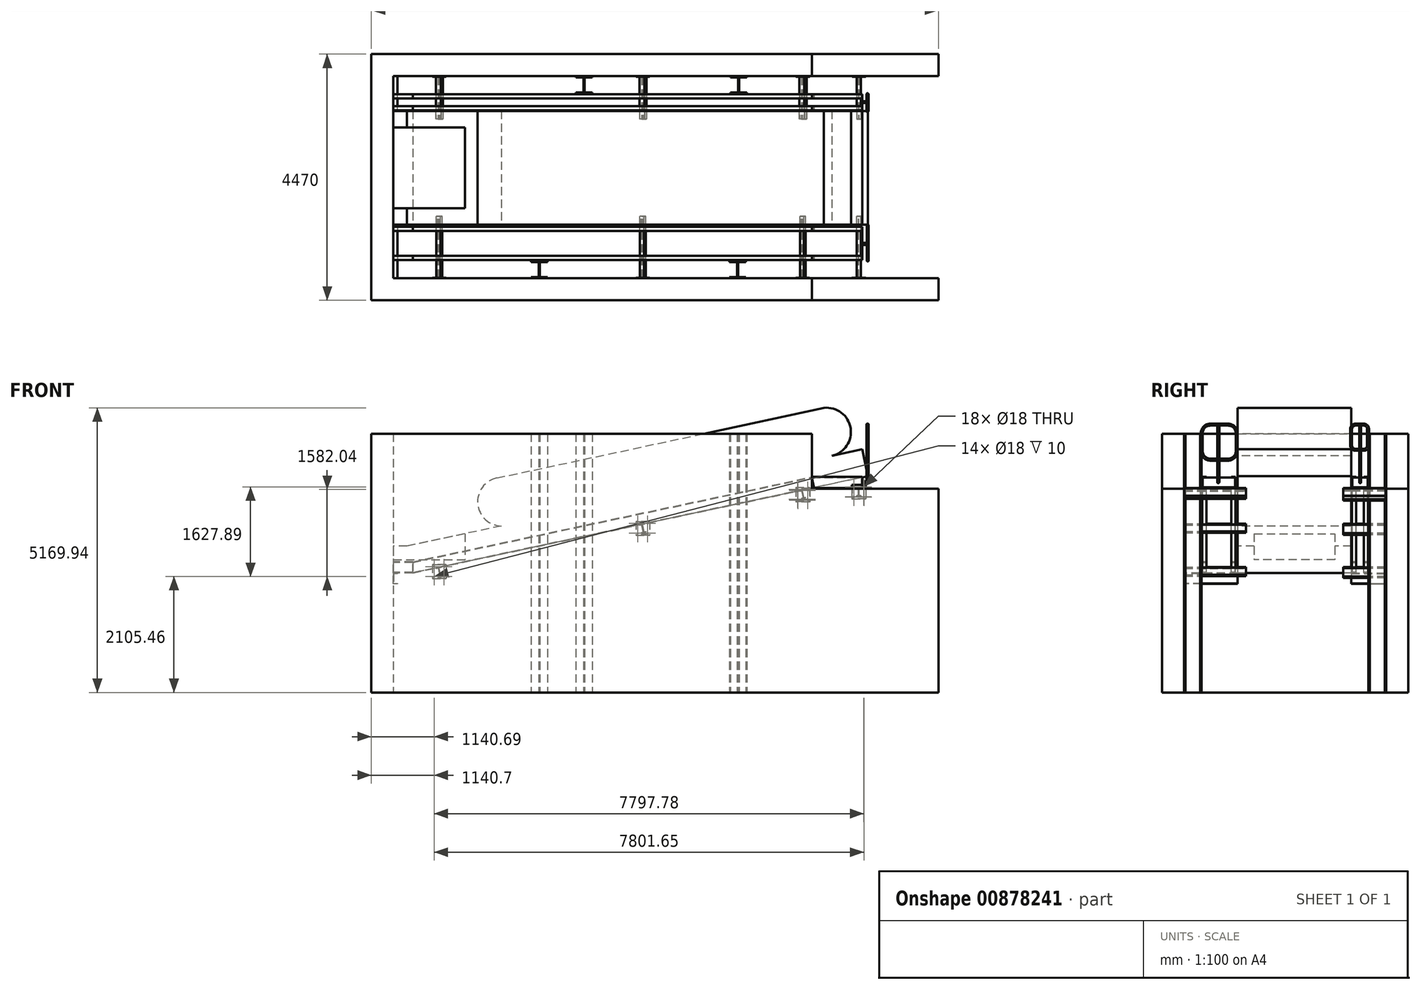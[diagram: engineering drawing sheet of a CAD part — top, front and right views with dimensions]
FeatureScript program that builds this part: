
annotation { "Feature Type Name" : "Feature", "Feature Type Description" : "" }
export const myFeature = defineFeature(function(context is Context, id is Id, definition is map)
    precondition{}
    {
        {
            var Q0;
            Q0=qCreatedBy(makeId("Top.planeOp"),FACE);
            var sketch = newSketch(context, id + "F0", { "sketchPlane" : qUnion([Q0])});
            skLineSegment(sketch, "E0", {"start": v(4950, 1835) * mm, "end": v(-4950, 1835) * mm});
            skLineSegment(sketch, "E1", {"start": v(-4950, 1835) * mm, "end": v(-4950, -1835) * mm});
            skLineSegment(sketch, "E2", {"start": v(-4950, -1835) * mm, "end": v(4950, -1835) * mm});
            skLineSegment(sketch, "E3", {"start": v(4950, -1835) * mm, "end": v(4950, -2235) * mm});
            skLineSegment(sketch, "E4", {"start": v(4950, -2235) * mm, "end": v(-5350, -2235) * mm});
            skLineSegment(sketch, "E5", {"start": v(-5350, -2235) * mm, "end": v(-5350, 2235) * mm});
            skLineSegment(sketch, "E6", {"start": v(-5350, 2235) * mm, "end": v(4950, 2235) * mm});
            skLineSegment(sketch, "E7", {"start": v(4950, 2235) * mm, "end": v(4950, 1835) * mm});
            skSolve(sketch);
        }
        {
            var Q0;
            Q0=qSketchRegion(id+"F0",true);
            extrude(context, id + "F1", {"entities" : qUnion([Q0]), "depth" : 4700 * mm, "offsetDistance" : 25 * mm});
        }
        {
            var Q0;
            Q0=makeQuery(id+"F1.opExtrude","SWEPT_FACE",FACE,{"disambiguationData":[OSD([sQuery(id+"F0.wireOp",EDGE,"E4")])]});
            var sketch = newSketch(context, id + "F2", { "sketchPlane" : qUnion([Q0])});
            skLineSegment(sketch, "E8", {"start": v(2650, 4700) * mm, "end": v(2650, 3700) * mm});
            skLineSegment(sketch, "E9", {"start": v(2650, 3700) * mm, "end": v(4950, 3700) * mm});
            skLineSegment(sketch, "E10", {"start": v(4950, 3700) * mm, "end": v(4950, 4700) * mm});
            skLineSegment(sketch, "E11", {"start": v(4950, 4700) * mm, "end": v(2650, 4700) * mm});
            skSolve(sketch);
        }
        {
            var Q0;
            Q0=qSketchRegion(id+"F2",true);
            extrude(context, id + "F3", {"entities" : qUnion([Q0]), "operationType" : NewBodyOperationType.REMOVE, "endBound" : BoundingType.THROUGH_ALL, "oppositeDirection" : true, "depth" : 25 * mm, "offsetDistance" : 25 * mm});
        }
        {
            var Q0;
            Q0=makeQuery(id+"F1.opExtrude","SWEPT_FACE",FACE,{"disambiguationData":[OSD([sQuery(id+"F0.wireOp",EDGE,"E2")])]});
            cPlane(context, id + "F4", {"entities" : qUnion([Q0]), "cplaneType" : CPlaneType.OFFSET, "offset" : 975 * mm, "width" : 150 * mm, "height" : 150 * mm});
        }
        {
            var Q0;
            Q0=qCreatedBy(id+"F4.planeOp",FACE);
            var sketch = newSketch(context, id + "F5", { "sketchPlane" : qUnion([Q0])});
            skLineSegment(sketch, "E12", {"start": v(0, 0) * mm, "end": v(4950, 0) * mm, "construction": true});
            skLineSegment(sketch, "E13", {"start": v(4950, 0) * mm, "end": v(4950, 2170) * mm, "construction": true});
            skLineSegment(sketch, "E14", {"start": v(3073.33, 3893.76) * mm, "end": v(-2866.18, 5167.23) * mm});
            skArc(sketch, "E15", {"start": v(2794.82, 3064.72) * mm, "mid": v(3398.25, 3323.3) * mm, "end": v(3073.33, 3893.76) * mm});
            skArc(sketch, "E16", {"start": v(-2866.18, 5167.23) * mm, "mid": v(-3350.27, 4800.3) * mm, "end": v(-3008.93, 4297.83) * mm});
            skLineSegment(sketch, "E17", {"start": v(-3008.93, 4297.83) * mm, "end": v(-3560.65, 4415.1) * mm});
            skLineSegment(sketch, "E18", {"start": v(-3560.65, 4415.1) * mm, "end": v(-3664.6, 3926.03) * mm});
            skLineSegment(sketch, "E19", {"start": v(-3664.6, 3926.03) * mm, "end": v(4600, 2170) * mm});
            skLineSegment(sketch, "E20", {"start": v(2794.82, 3064.72) * mm, "end": v(4703.92, 2658.93) * mm});
            skLineSegment(sketch, "E21", {"start": v(4950, 2658.93) * mm, "end": v(4950, 2170) * mm});
            skLineSegment(sketch, "E22", {"start": v(4703.92, 2658.93) * mm, "end": v(4950, 2658.93) * mm});
            skLineSegment(sketch, "E23", {"start": v(4600, 2170) * mm, "end": v(4950, 2170) * mm});
            skSolve(sketch);
        }
        {
            var Q0;
            Q0=qSketchRegion(id+"F5",true);
            extrude(context, id + "F6", {"entities" : qUnion([Q0]), "depth" : 2065 * mm, "offsetDistance" : 25 * mm});
        }
        {
            var Q0;
            Q0=qCreatedBy(makeId("Top.planeOp"),FACE);
            var sketch = newSketch(context, id + "F7", { "sketchPlane" : qUnion([Q0])});
            skLineSegment(sketch, "E24", {"start": v(-2450, -1835) * mm, "end": v(-2450, -1810) * mm});
            skLineSegment(sketch, "E25", {"start": v(-2450, -1810) * mm, "end": v(-2310, -1810) * mm});
            skLineSegment(sketch, "E26", {"start": v(-2290, -1540) * mm, "end": v(-2290, -1810) * mm});
            skLineSegment(sketch, "E27", {"start": v(-2290, -1810) * mm, "end": v(-2150, -1810) * mm});
            skLineSegment(sketch, "E28", {"start": v(-2150, -1810) * mm, "end": v(-2150, -1835) * mm});
            skLineSegment(sketch, "E29", {"start": v(-2150, -1835) * mm, "end": v(-2450, -1835) * mm});
            skLineSegment(sketch, "E30", {"start": v(-2310, -1810) * mm, "end": v(-2310, -1540) * mm});
            skLineSegment(sketch, "E31", {"start": v(-2310, -1540) * mm, "end": v(-2450, -1540) * mm});
            skLineSegment(sketch, "E32", {"start": v(-2450, -1540) * mm, "end": v(-2450, -1515) * mm});
            skLineSegment(sketch, "E33", {"start": v(-2150, -1515) * mm, "end": v(-2450, -1515) * mm});
            skLineSegment(sketch, "E34", {"start": v(-2290, -1540) * mm, "end": v(-2150, -1540) * mm});
            skLineSegment(sketch, "E35", {"start": v(-2150, -1540) * mm, "end": v(-2150, -1515) * mm});
            skLineSegment(sketch, "E36.MirrorCS", {"start": v(1150, -1540) * mm, "end": v(1150, -1515) * mm});
            skLineSegment(sketch, "E37.MirrorCS", {"start": v(1450, -1540) * mm, "end": v(1450, -1515) * mm});
            skLineSegment(sketch, "E38.MirrorCS", {"start": v(1150, -1810) * mm, "end": v(1150, -1835) * mm});
            skLineSegment(sketch, "E39.MirrorCS", {"start": v(1450, -1835) * mm, "end": v(1450, -1810) * mm});
            skLineSegment(sketch, "E40.MirrorCS", {"start": v(1290, -1540) * mm, "end": v(1150, -1540) * mm});
            skLineSegment(sketch, "E41.MirrorCS", {"start": v(1290, -1540) * mm, "end": v(1290, -1810) * mm});
            skLineSegment(sketch, "E42.MirrorCS", {"start": v(1310, -1540) * mm, "end": v(1450, -1540) * mm});
            skLineSegment(sketch, "E43.MirrorCS", {"start": v(1290, -1810) * mm, "end": v(1150, -1810) * mm});
            skLineSegment(sketch, "E44.MirrorCS", {"start": v(1450, -1810) * mm, "end": v(1310, -1810) * mm});
            skLineSegment(sketch, "E45.MirrorCS", {"start": v(1150, -1835) * mm, "end": v(1450, -1835) * mm});
            skLineSegment(sketch, "E46.MirrorCS", {"start": v(1150, -1515) * mm, "end": v(1450, -1515) * mm});
            skLineSegment(sketch, "E47.MirrorCS", {"start": v(1310, -1810) * mm, "end": v(1310, -1540) * mm});
            skLineSegment(sketch, "E48", {"start": v(0, 0) * mm, "end": v(-354.85, 0) * mm, "construction": true});
            skLineSegment(sketch, "E49", {"start": v(-1640, 1515) * mm, "end": v(-1640, 1540) * mm});
            skLineSegment(sketch, "E50", {"start": v(-1640, 1540) * mm, "end": v(-1500, 1540) * mm});
            skLineSegment(sketch, "E51", {"start": v(-1480, 1810) * mm, "end": v(-1480, 1540) * mm});
            skLineSegment(sketch, "E52", {"start": v(-1480, 1540) * mm, "end": v(-1340, 1540) * mm});
            skLineSegment(sketch, "E53", {"start": v(-1340, 1540) * mm, "end": v(-1340, 1515) * mm});
            skLineSegment(sketch, "E54", {"start": v(-1340, 1515) * mm, "end": v(-1640, 1515) * mm});
            skLineSegment(sketch, "E55", {"start": v(-1500, 1540) * mm, "end": v(-1500, 1810) * mm});
            skLineSegment(sketch, "E56", {"start": v(-1500, 1810) * mm, "end": v(-1640, 1810) * mm});
            skLineSegment(sketch, "E57", {"start": v(-1640, 1810) * mm, "end": v(-1640, 1835) * mm});
            skLineSegment(sketch, "E58", {"start": v(-1340, 1835) * mm, "end": v(-1640, 1835) * mm});
            skLineSegment(sketch, "E59", {"start": v(-1480, 1810) * mm, "end": v(-1340, 1810) * mm});
            skLineSegment(sketch, "E60", {"start": v(-1340, 1810) * mm, "end": v(-1340, 1835) * mm});
            skLineSegment(sketch, "E61", {"start": v(1170, 1515) * mm, "end": v(1170, 1540) * mm});
            skLineSegment(sketch, "E62", {"start": v(1170, 1540) * mm, "end": v(1310, 1540) * mm});
            skLineSegment(sketch, "E63", {"start": v(1330, 1810) * mm, "end": v(1330, 1540) * mm});
            skLineSegment(sketch, "E64", {"start": v(1330, 1540) * mm, "end": v(1470, 1540) * mm});
            skLineSegment(sketch, "E65", {"start": v(1470, 1540) * mm, "end": v(1470, 1515) * mm});
            skLineSegment(sketch, "E66", {"start": v(1470, 1515) * mm, "end": v(1170, 1515) * mm});
            skLineSegment(sketch, "E67", {"start": v(1310, 1540) * mm, "end": v(1310, 1810) * mm});
            skLineSegment(sketch, "E68", {"start": v(1310, 1810) * mm, "end": v(1170, 1810) * mm});
            skLineSegment(sketch, "E69", {"start": v(1170, 1810) * mm, "end": v(1170, 1835) * mm});
            skLineSegment(sketch, "E70", {"start": v(1470, 1835) * mm, "end": v(1170, 1835) * mm});
            skLineSegment(sketch, "E71", {"start": v(1330, 1810) * mm, "end": v(1470, 1810) * mm});
            skLineSegment(sketch, "E72", {"start": v(1470, 1810) * mm, "end": v(1470, 1835) * mm});
            skSolve(sketch);
        }
        {
            var Q0;
            Q0=qSketchRegion(id+"F7",true);
            extrude(context, id + "F8", {"entities" : qUnion([Q0]), "depth" : 4700 * mm, "offsetDistance" : 25 * mm});
        }
        {
            var Q0;
            Q0=makeQuery(id+"F6.opExtrude","CAP_FACE",FACE,{"disambiguationData":[OSD([sQuery(id+"F5.wireOp",EDGE,"E14"),sQuery(id+"F5.wireOp",EDGE,"E15"),sQuery(id+"F5.wireOp",EDGE,"E16"),sQuery(id+"F5.wireOp",EDGE,"oLefBTFz-qkPp-oevc-OMQC-yi734GtDL7CI"),sQuery(id+"F5.wireOp",EDGE,"Q5l5viEM-SpAK-wrV8-5FxA-7hyHcSo3zPGG"),sQuery(id+"F5.wireOp",EDGE,"E17"),sQuery(id+"F5.wireOp",EDGE,"Mw7AiCCQ-qxsM-Rx6K-VWYf-NFiuKVvHO99K"),sQuery(id+"F5.wireOp",EDGE,"wAlzpoZe-HTRn-fX5u-Gcly-RZiGOCXCuHdc")])],"isStart":true});
            var sketch = newSketch(context, id + "F9", { "sketchPlane" : qUnion([Q0])});
            skLineSegment(sketch, "E73", {"start": v(-434.88, 3054.99) * mm, "end": v(-400.65, 3062.26) * mm});
            skLineSegment(sketch, "E74", {"start": v(-400.65, 3062.26) * mm, "end": v(-399.2, 3055.41) * mm});
            skLineSegment(sketch, "E75", {"start": v(-399.2, 3055.41) * mm, "end": v(-433.43, 3048.14) * mm});
            skLineSegment(sketch, "E76", {"start": v(-433.43, 3048.14) * mm, "end": v(-405.16, 2915.11) * mm});
            skLineSegment(sketch, "E77", {"start": v(-405.16, 2915.11) * mm, "end": v(-370.93, 2922.38) * mm});
            skLineSegment(sketch, "E78", {"start": v(-370.93, 2922.38) * mm, "end": v(-369.47, 2915.54) * mm});
            skLineSegment(sketch, "E79", {"start": v(-369.47, 2915.54) * mm, "end": v(-442.83, 2899.95) * mm});
            skLineSegment(sketch, "E80", {"start": v(-442.83, 2899.95) * mm, "end": v(-444.29, 2906.8) * mm});
            skLineSegment(sketch, "E81", {"start": v(-444.29, 2906.8) * mm, "end": v(-410.05, 2914.07) * mm});
            skLineSegment(sketch, "E82", {"start": v(-410.05, 2914.07) * mm, "end": v(-438.32, 3047.1) * mm});
            skLineSegment(sketch, "E83", {"start": v(-438.32, 3047.1) * mm, "end": v(-472.55, 3039.83) * mm});
            skLineSegment(sketch, "E84", {"start": v(-472.55, 3039.83) * mm, "end": v(-474, 3046.67) * mm});
            skLineSegment(sketch, "E85", {"start": v(-474, 3046.67) * mm, "end": v(-400.65, 3062.26) * mm});
            skLineSegment(sketch, "E86.MirrorCS", {"start": v(-4128.54, 2263.02) * mm, "end": v(-4094.3, 2270.3) * mm});
            skLineSegment(sketch, "E87.MirrorCS", {"start": v(-4167.66, 2254.7) * mm, "end": v(-4133.43, 2261.98) * mm});
            skLineSegment(sketch, "E88.MirrorCS", {"start": v(-4169.12, 2261.55) * mm, "end": v(-4167.66, 2254.7) * mm});
            skLineSegment(sketch, "E89.MirrorCS", {"start": v(-4105.16, 2128.95) * mm, "end": v(-4139.4, 2121.67) * mm});
            skLineSegment(sketch, "E90.MirrorCS", {"start": v(-4134.88, 2268.83) * mm, "end": v(-4169.12, 2261.55) * mm});
            skLineSegment(sketch, "E91.MirrorCS", {"start": v(-4139.4, 2121.67) * mm, "end": v(-4137.94, 2114.83) * mm});
            skLineSegment(sketch, "E92.MirrorCS", {"start": v(-4066.04, 2137.26) * mm, "end": v(-4100.27, 2129.99) * mm});
            skLineSegment(sketch, "E93.MirrorCS", {"start": v(-4095.76, 2277.14) * mm, "end": v(-4169.12, 2261.55) * mm});
            skLineSegment(sketch, "E94.MirrorCS", {"start": v(-4137.94, 2114.83) * mm, "end": v(-4064.58, 2130.42) * mm});
            skLineSegment(sketch, "E95.MirrorCS", {"start": v(-4064.58, 2130.42) * mm, "end": v(-4066.04, 2137.26) * mm});
            skLineSegment(sketch, "E96.MirrorCS", {"start": v(-4094.3, 2270.3) * mm, "end": v(-4095.76, 2277.14) * mm});
            skLineSegment(sketch, "E97.MirrorCS", {"start": v(-4133.43, 2261.98) * mm, "end": v(-4105.16, 2128.95) * mm});
            skLineSegment(sketch, "E98.MirrorCS", {"start": v(-4100.27, 2129.99) * mm, "end": v(-4128.54, 2263.02) * mm});
            skLineSegment(sketch, "E99.MirrorCS", {"start": v(2429.47, 3663.6) * mm, "end": v(2430.93, 3656.75) * mm});
            skLineSegment(sketch, "E100.MirrorCS", {"start": v(2504.3, 3672.34) * mm, "end": v(2502.84, 3679.18) * mm});
            skLineSegment(sketch, "E101.MirrorCS", {"start": v(2430.93, 3656.75) * mm, "end": v(2465.16, 3664.02) * mm});
            skLineSegment(sketch, "E102.MirrorCS", {"start": v(2463.7, 3670.87) * mm, "end": v(2429.47, 3663.6) * mm});
            skLineSegment(sketch, "E103.MirrorCS", {"start": v(2502.84, 3679.18) * mm, "end": v(2429.47, 3663.6) * mm});
            skLineSegment(sketch, "E104.MirrorCS", {"start": v(2459.2, 3523.72) * mm, "end": v(2460.65, 3516.87) * mm});
            skLineSegment(sketch, "E105.MirrorCS", {"start": v(2534.01, 3532.46) * mm, "end": v(2532.56, 3539.3) * mm});
            skLineSegment(sketch, "E106.MirrorCS", {"start": v(2470.05, 3665.06) * mm, "end": v(2504.3, 3672.34) * mm});
            skLineSegment(sketch, "E107.MirrorCS", {"start": v(2460.65, 3516.87) * mm, "end": v(2534.01, 3532.46) * mm});
            skLineSegment(sketch, "E108.MirrorCS", {"start": v(2493.43, 3531) * mm, "end": v(2459.2, 3523.72) * mm});
            skLineSegment(sketch, "E109.MirrorCS", {"start": v(2532.56, 3539.3) * mm, "end": v(2498.32, 3532.03) * mm});
            skLineSegment(sketch, "E110.MirrorCS", {"start": v(2465.16, 3664.02) * mm, "end": v(2493.43, 3531) * mm});
            skLineSegment(sketch, "E111.MirrorCS", {"start": v(2498.32, 3532.03) * mm, "end": v(2470.05, 3665.06) * mm});
            skLineSegment(sketch, "E112", {"start": v(-4134.88, 2268.83) * mm, "end": v(-4134.88, 2268.83) * mm});
            skLineSegment(sketch, "E113", {"start": v(-434.88, 3054.99) * mm, "end": v(-434.88, 3054.99) * mm});
            skLineSegment(sketch, "E114", {"start": v(2463.7, 3670.87) * mm, "end": v(2463.7, 3670.87) * mm});
            skLineSegment(sketch, "E115", {"start": v(3664.6, 3926.03) * mm, "end": v(2664.6, 3926.03) * mm, "construction": true});
            skLineSegment(sketch, "E116", {"start": v(2664.6, 3926.03) * mm, "end": v(2420.07, 3874.07) * mm, "construction": true});
            skLineSegment(sketch, "E117", {"start": v(2420.07, 3874.07) * mm, "end": v(2463.26, 3670.77) * mm, "construction": true});
            skLineSegment(sketch, "E118.MirrorCS", {"start": v(3459.6, 3713.73) * mm, "end": v(3459.6, 3706.73) * mm});
            skLineSegment(sketch, "E119.MirrorCS", {"start": v(3534.6, 3706.73) * mm, "end": v(3534.6, 3713.73) * mm});
            skLineSegment(sketch, "E120.MirrorCS", {"start": v(3459.6, 3706.73) * mm, "end": v(3494.6, 3706.73) * mm});
            skLineSegment(sketch, "E121.MirrorCS", {"start": v(3496.14, 3713.73) * mm, "end": v(3459.6, 3713.73) * mm});
            skLineSegment(sketch, "E122.MirrorCS", {"start": v(3534.6, 3713.73) * mm, "end": v(3459.6, 3713.73) * mm});
            skLineSegment(sketch, "E123.MirrorCS", {"start": v(3459.6, 3570.73) * mm, "end": v(3459.6, 3563.73) * mm});
            skLineSegment(sketch, "E124.MirrorCS", {"start": v(3534.6, 3563.73) * mm, "end": v(3534.6, 3570.73) * mm});
            skLineSegment(sketch, "E125.MirrorCS", {"start": v(3499.6, 3706.73) * mm, "end": v(3534.6, 3706.73) * mm});
            skLineSegment(sketch, "E126.MirrorCS", {"start": v(3459.6, 3563.73) * mm, "end": v(3534.6, 3563.73) * mm});
            skLineSegment(sketch, "E127.MirrorCS", {"start": v(3494.6, 3570.73) * mm, "end": v(3459.6, 3570.73) * mm});
            skLineSegment(sketch, "E128.MirrorCS", {"start": v(3534.6, 3570.73) * mm, "end": v(3499.6, 3570.73) * mm});
            skLineSegment(sketch, "E129.MirrorCS", {"start": v(3499.6, 3570.73) * mm, "end": v(3499.6, 3706.73) * mm});
            skLineSegment(sketch, "E130", {"start": v(3494.6, 3706.73) * mm, "end": v(3494.6, 3570.73) * mm});
            skSolve(sketch);
        }
        {
            var Q0;
            Q0 = qSketchRegion(id + "F9", true);
            extrude(context, id + "F10", {"entities" : qUnion([Q0]), "operationType" : NewBodyOperationType.ADD, "depth" : 965 * mm, "offsetDistance" : 25 * mm, "hasSecondDirection" : true, "secondDirectionOppositeDirection" : true, "secondDirectionDepth" : 150 * mm});
        }
        {
            var Q0;
            Q0=makeQuery(id+"F10.opExtrude","CAP_FACE",FACE,{"disambiguationData":[OSD([sQuery(id+"F9.wireOp",EDGE,"E99.MirrorCS"),sQuery(id+"F9.wireOp",EDGE,"E100.MirrorCS"),sQuery(id+"F9.wireOp",EDGE,"E101.MirrorCS"),sQuery(id+"F9.wireOp",EDGE,"E103.MirrorCS"),sQuery(id+"F9.wireOp",EDGE,"E104.MirrorCS"),sQuery(id+"F9.wireOp",EDGE,"E105.MirrorCS"),sQuery(id+"F9.wireOp",EDGE,"E106.MirrorCS"),sQuery(id+"F9.wireOp",EDGE,"E107.MirrorCS"),sQuery(id+"F9.wireOp",EDGE,"E108.MirrorCS"),sQuery(id+"F9.wireOp",EDGE,"E109.MirrorCS"),sQuery(id+"F9.wireOp",EDGE,"E110.MirrorCS"),sQuery(id+"F9.wireOp",EDGE,"E111.MirrorCS")])],"isStart":false});
            var sketch = newSketch(context, id + "F11", { "sketchPlane" : qUnion([Q0])});
            skLineSegment(sketch, "E131.bottom", {"start": v(2354.3, 3722.5) * mm, "end": v(2604.3, 3722.5) * mm});
            skLineSegment(sketch, "E131.top", {"start": v(2354.3, 3472.5) * mm, "end": v(2604.3, 3472.5) * mm});
            skLineSegment(sketch, "E131.left", {"start": v(2354.3, 3722.5) * mm, "end": v(2354.3, 3472.5) * mm});
            skLineSegment(sketch, "E131.right", {"start": v(2604.3, 3722.5) * mm, "end": v(2604.3, 3472.5) * mm});
            skLineSegment(sketch, "E132", {"start": v(2479.3, 3597.5) * mm, "end": v(2479.3, 3576.9) * mm, "construction": true});
            skLineSegment(sketch, "E133", {"start": v(2479.3, 3597.5) * mm, "end": v(2510.05, 3597.5) * mm, "construction": true});
            skCircle(sketch, "E134", {"center": v(2389.3, 3687.5) * mm, "radius": 9 * mm});
            skCircle(sketch, "E135", {"center": v(2389.3, 3507.5) * mm, "radius": 9 * mm});
            skCircle(sketch, "E136", {"center": v(2569.3, 3687.5) * mm, "radius": 9 * mm});
            skCircle(sketch, "E137", {"center": v(2569.3, 3507.5) * mm, "radius": 9 * mm});
            skLineSegment(sketch, "E138.bottom", {"start": v(-549.18, 3105.59) * mm, "end": v(-299.18, 3105.59) * mm});
            skLineSegment(sketch, "E138.top", {"start": v(-549.18, 2855.59) * mm, "end": v(-299.18, 2855.59) * mm});
            skLineSegment(sketch, "E138.left", {"start": v(-549.18, 3105.59) * mm, "end": v(-549.18, 2855.59) * mm});
            skLineSegment(sketch, "E138.right", {"start": v(-299.18, 3105.59) * mm, "end": v(-299.18, 2855.59) * mm});
            skLineSegment(sketch, "E139", {"start": v(-424.18, 2980.59) * mm, "end": v(-424.18, 2959.98) * mm, "construction": true});
            skLineSegment(sketch, "E140", {"start": v(-424.18, 2980.59) * mm, "end": v(-393.43, 2980.59) * mm, "construction": true});
            skCircle(sketch, "E141", {"center": v(-514.18, 3070.59) * mm, "radius": 9 * mm});
            skCircle(sketch, "E142", {"center": v(-514.18, 2890.59) * mm, "radius": 9 * mm});
            skCircle(sketch, "E143", {"center": v(-334.18, 3070.59) * mm, "radius": 9 * mm});
            skCircle(sketch, "E144", {"center": v(-334.18, 2890.59) * mm, "radius": 9 * mm});
            skLineSegment(sketch, "E145.bottom", {"start": v(-4244.3, 2320.46) * mm, "end": v(-3994.3, 2320.46) * mm});
            skLineSegment(sketch, "E145.top", {"start": v(-4244.3, 2070.46) * mm, "end": v(-3994.3, 2070.46) * mm});
            skLineSegment(sketch, "E145.left", {"start": v(-4244.3, 2320.46) * mm, "end": v(-4244.3, 2070.46) * mm});
            skLineSegment(sketch, "E145.right", {"start": v(-3994.3, 2320.46) * mm, "end": v(-3994.3, 2070.46) * mm});
            skLineSegment(sketch, "E146", {"start": v(-4119.3, 2195.46) * mm, "end": v(-4119.3, 2174.86) * mm, "construction": true});
            skLineSegment(sketch, "E147", {"start": v(-4119.3, 2195.46) * mm, "end": v(-4088.55, 2195.46) * mm, "construction": true});
            skCircle(sketch, "E148", {"center": v(-4209.3, 2285.46) * mm, "radius": 9 * mm});
            skCircle(sketch, "E149", {"center": v(-4209.3, 2105.46) * mm, "radius": 9 * mm});
            skCircle(sketch, "E150", {"center": v(-4029.3, 2285.46) * mm, "radius": 9 * mm});
            skCircle(sketch, "E151", {"center": v(-4029.3, 2105.46) * mm, "radius": 9 * mm});
            skLineSegment(sketch, "E152.bottom", {"start": v(3373.49, 3768.35) * mm, "end": v(3623.49, 3768.35) * mm});
            skLineSegment(sketch, "E152.top", {"start": v(3373.49, 3518.35) * mm, "end": v(3623.49, 3518.35) * mm});
            skLineSegment(sketch, "E152.left", {"start": v(3373.49, 3768.35) * mm, "end": v(3373.49, 3518.35) * mm});
            skLineSegment(sketch, "E152.right", {"start": v(3623.49, 3768.35) * mm, "end": v(3623.49, 3518.35) * mm});
            skLineSegment(sketch, "E153", {"start": v(3498.49, 3643.35) * mm, "end": v(3498.49, 3622.74) * mm, "construction": true});
            skLineSegment(sketch, "E154", {"start": v(3498.49, 3643.35) * mm, "end": v(3529.24, 3643.35) * mm, "construction": true});
            skCircle(sketch, "E155", {"center": v(3408.49, 3733.35) * mm, "radius": 9 * mm});
            skCircle(sketch, "E156", {"center": v(3408.49, 3553.35) * mm, "radius": 9 * mm});
            skCircle(sketch, "E157", {"center": v(3588.49, 3733.35) * mm, "radius": 9 * mm});
            skCircle(sketch, "E158", {"center": v(3588.49, 3553.35) * mm, "radius": 9 * mm});
            skSolve(sketch);
        }
        {
            var Q0;
            Q0 = qSketchRegion(id + "F11", true);
            extrude(context, id + "F12", {"entities" : qUnion([Q0]), "operationType" : NewBodyOperationType.ADD, "depth" : 10 * mm, "offsetDistance" : 25 * mm});
        }
        {
            var Q0;
            Q0=makeQuery(id+"F6.opExtrude","CAP_FACE",FACE,{"disambiguationData":[OSD([sQuery(id+"F5.wireOp",EDGE,"E14"),sQuery(id+"F5.wireOp",EDGE,"E15"),sQuery(id+"F5.wireOp",EDGE,"E16"),sQuery(id+"F5.wireOp",EDGE,"oLefBTFz-qkPp-oevc-OMQC-yi734GtDL7CI"),sQuery(id+"F5.wireOp",EDGE,"Q5l5viEM-SpAK-wrV8-5FxA-7hyHcSo3zPGG"),sQuery(id+"F5.wireOp",EDGE,"E17"),sQuery(id+"F5.wireOp",EDGE,"Mw7AiCCQ-qxsM-Rx6K-VWYf-NFiuKVvHO99K"),sQuery(id+"F5.wireOp",EDGE,"wAlzpoZe-HTRn-fX5u-Gcly-RZiGOCXCuHdc")])],"isStart":false});
            var sketch = newSketch(context, id + "F13", { "sketchPlane" : qUnion([Q0])});
            skLineSegment(sketch, "E159.MirrorCS", {"start": v(-2511.47, 3682.12) * mm, "end": v(-2513.27, 3673.67) * mm});
            skLineSegment(sketch, "E160.MirrorCS", {"start": v(-2422.67, 3654.4) * mm, "end": v(-2420.87, 3662.86) * mm});
            skLineSegment(sketch, "E161.MirrorCS", {"start": v(-2513.27, 3673.67) * mm, "end": v(-2470.99, 3664.68) * mm});
            skLineSegment(sketch, "E162.MirrorCS", {"start": v(-2548.2, 3509.38) * mm, "end": v(-2550, 3500.92) * mm});
            skLineSegment(sketch, "E163.MirrorCS", {"start": v(-2459.4, 3481.66) * mm, "end": v(-2457.6, 3490.11) * mm});
            skLineSegment(sketch, "E164.MirrorCS", {"start": v(-2464.95, 3663.4) * mm, "end": v(-2422.67, 3654.4) * mm});
            skLineSegment(sketch, "E165.MirrorCS", {"start": v(-2550, 3500.92) * mm, "end": v(-2459.4, 3481.66) * mm});
            skLineSegment(sketch, "E166.MirrorCS", {"start": v(-2505.92, 3500.39) * mm, "end": v(-2548.2, 3509.38) * mm});
            skLineSegment(sketch, "E167.MirrorCS", {"start": v(-2457.6, 3490.11) * mm, "end": v(-2499.88, 3499.1) * mm});
            skLineSegment(sketch, "E168.MirrorCS", {"start": v(-2470.99, 3664.68) * mm, "end": v(-2505.92, 3500.39) * mm});
            skLineSegment(sketch, "E169.MirrorCS", {"start": v(-2499.88, 3499.1) * mm, "end": v(-2464.95, 3663.4) * mm});
            skLineSegment(sketch, "E170", {"start": v(-2511.47, 3682.12) * mm, "end": v(-2420.87, 3662.86) * mm});
            skLineSegment(sketch, "E171.MirrorCS", {"start": v(392.09, 3064.09) * mm, "end": v(390.29, 3055.63) * mm});
            skLineSegment(sketch, "E172.MirrorCS", {"start": v(480.89, 3036.37) * mm, "end": v(482.69, 3044.82) * mm});
            skLineSegment(sketch, "E173.MirrorCS", {"start": v(390.29, 3055.63) * mm, "end": v(432.57, 3046.64) * mm});
            skLineSegment(sketch, "E174.MirrorCS", {"start": v(355.35, 2891.34) * mm, "end": v(353.56, 2882.89) * mm});
            skLineSegment(sketch, "E175.MirrorCS", {"start": v(444.16, 2863.62) * mm, "end": v(445.95, 2872.08) * mm});
            skLineSegment(sketch, "E176.MirrorCS", {"start": v(438.6, 3045.36) * mm, "end": v(480.89, 3036.37) * mm});
            skLineSegment(sketch, "E177.MirrorCS", {"start": v(353.56, 2882.89) * mm, "end": v(444.16, 2863.62) * mm});
            skLineSegment(sketch, "E178.MirrorCS", {"start": v(397.63, 2882.35) * mm, "end": v(355.35, 2891.34) * mm});
            skLineSegment(sketch, "E179.MirrorCS", {"start": v(445.95, 2872.08) * mm, "end": v(403.67, 2881.07) * mm});
            skLineSegment(sketch, "E180.MirrorCS", {"start": v(432.57, 3046.64) * mm, "end": v(397.63, 2882.35) * mm});
            skLineSegment(sketch, "E181.MirrorCS", {"start": v(403.67, 2881.07) * mm, "end": v(438.6, 3045.36) * mm});
            skLineSegment(sketch, "E182", {"start": v(392.09, 3064.09) * mm, "end": v(482.69, 3044.82) * mm});
            skLineSegment(sketch, "E183.MirrorCS", {"start": v(4087.2, 2279.02) * mm, "end": v(4085.4, 2270.57) * mm});
            skLineSegment(sketch, "E184.MirrorCS", {"start": v(4176, 2251.3) * mm, "end": v(4177.8, 2259.76) * mm});
            skLineSegment(sketch, "E185.MirrorCS", {"start": v(4085.4, 2270.57) * mm, "end": v(4127.69, 2261.58) * mm});
            skLineSegment(sketch, "E186.MirrorCS", {"start": v(4050.47, 2106.28) * mm, "end": v(4048.67, 2097.82) * mm});
            skLineSegment(sketch, "E187.MirrorCS", {"start": v(4139.28, 2078.55) * mm, "end": v(4141.07, 2087.01) * mm});
            skLineSegment(sketch, "E188.MirrorCS", {"start": v(4133.73, 2260.3) * mm, "end": v(4176, 2251.3) * mm});
            skLineSegment(sketch, "E189.MirrorCS", {"start": v(4048.67, 2097.82) * mm, "end": v(4139.28, 2078.55) * mm});
            skLineSegment(sketch, "E190.MirrorCS", {"start": v(4092.75, 2097.29) * mm, "end": v(4050.47, 2106.28) * mm});
            skLineSegment(sketch, "E191.MirrorCS", {"start": v(4141.07, 2087.01) * mm, "end": v(4098.82, 2096) * mm});
            skLineSegment(sketch, "E192.MirrorCS", {"start": v(4127.69, 2261.58) * mm, "end": v(4092.75, 2097.29) * mm});
            skLineSegment(sketch, "E193.MirrorCS", {"start": v(4098.82, 2096) * mm, "end": v(4133.73, 2260.3) * mm});
            skLineSegment(sketch, "E194", {"start": v(4087.2, 2279.02) * mm, "end": v(4177.8, 2259.76) * mm});
            skLineSegment(sketch, "E195", {"start": v(-3664.6, 3926.03) * mm, "end": v(-3664.6, 3714) * mm, "construction": true});
            skLineSegment(sketch, "E196", {"start": v(-3664.6, 3714) * mm, "end": v(-3534.6, 3714) * mm, "construction": true});
            skLineSegment(sketch, "E197", {"start": v(-3664.6, 3926.03) * mm, "end": v(-2664.6, 3926.03) * mm, "construction": true});
            skLineSegment(sketch, "E198", {"start": v(-2664.6, 3926.03) * mm, "end": v(-2420.07, 3874.07) * mm, "construction": true});
            skLineSegment(sketch, "E199", {"start": v(-2420.07, 3874.07) * mm, "end": v(-2420.07, 3661.6) * mm, "construction": true});
            skLineSegment(sketch, "E200.MirrorCS", {"start": v(-3534.58, 3713.73) * mm, "end": v(-3534.58, 3706.73) * mm});
            skLineSegment(sketch, "E201.MirrorCS", {"start": v(-3459.58, 3706.72) * mm, "end": v(-3459.58, 3713.72) * mm});
            skLineSegment(sketch, "E202.MirrorCS", {"start": v(-3534.58, 3706.73) * mm, "end": v(-3499.58, 3706.72) * mm});
            skLineSegment(sketch, "E203.MirrorCS", {"start": v(-3498.05, 3713.72) * mm, "end": v(-3534.58, 3713.73) * mm});
            skLineSegment(sketch, "E204.MirrorCS", {"start": v(-3459.58, 3713.72) * mm, "end": v(-3534.58, 3713.73) * mm});
            skLineSegment(sketch, "E205.MirrorCS", {"start": v(-3534.6, 3570.73) * mm, "end": v(-3534.6, 3563.73) * mm});
            skLineSegment(sketch, "E206.MirrorCS", {"start": v(-3459.6, 3563.72) * mm, "end": v(-3459.6, 3570.72) * mm});
            skLineSegment(sketch, "E207.MirrorCS", {"start": v(-3494.58, 3706.72) * mm, "end": v(-3459.58, 3706.72) * mm});
            skLineSegment(sketch, "E208.MirrorCS", {"start": v(-3534.6, 3563.73) * mm, "end": v(-3459.6, 3563.72) * mm});
            skLineSegment(sketch, "E209.MirrorCS", {"start": v(-3499.6, 3570.72) * mm, "end": v(-3534.6, 3570.73) * mm});
            skLineSegment(sketch, "E210.MirrorCS", {"start": v(-3459.6, 3570.72) * mm, "end": v(-3494.6, 3570.72) * mm});
            skLineSegment(sketch, "E211.MirrorCS", {"start": v(-3494.6, 3570.72) * mm, "end": v(-3494.58, 3706.72) * mm});
            skLineSegment(sketch, "E212", {"start": v(-3499.58, 3706.72) * mm, "end": v(-3499.6, 3570.72) * mm});
            skSolve(sketch);
        }
        {
            var Q0;
            Q0 = qSketchRegion(id + "F13", true);
            extrude(context, id + "F14", {"entities" : qUnion([Q0]), "operationType" : NewBodyOperationType.ADD, "depth" : 620 * mm, "offsetDistance" : 25 * mm, "hasSecondDirection" : true, "secondDirectionOppositeDirection" : true, "secondDirectionDepth" : 150 * mm});
        }
        {
            var Q0;
            Q0=makeQuery(id+"F14.opExtrude","CAP_FACE",FACE,{"disambiguationData":[OSD([sQuery(id+"F13.wireOp",EDGE,"E159.MirrorCS"),sQuery(id+"F13.wireOp",EDGE,"E160.MirrorCS"),sQuery(id+"F13.wireOp",EDGE,"E161.MirrorCS"),sQuery(id+"F13.wireOp",EDGE,"E162.MirrorCS"),sQuery(id+"F13.wireOp",EDGE,"E163.MirrorCS"),sQuery(id+"F13.wireOp",EDGE,"E164.MirrorCS"),sQuery(id+"F13.wireOp",EDGE,"E165.MirrorCS"),sQuery(id+"F13.wireOp",EDGE,"E166.MirrorCS"),sQuery(id+"F13.wireOp",EDGE,"E167.MirrorCS"),sQuery(id+"F13.wireOp",EDGE,"E168.MirrorCS"),sQuery(id+"F13.wireOp",EDGE,"E169.MirrorCS"),sQuery(id+"F13.wireOp",EDGE,"E170")])],"isStart":false});
            var sketch = newSketch(context, id + "F15", { "sketchPlane" : qUnion([Q0])});
            skLineSegment(sketch, "E213.bottom", {"start": v(299.18, 3105.59) * mm, "end": v(549.18, 3105.59) * mm});
            skLineSegment(sketch, "E213.top", {"start": v(299.18, 2855.59) * mm, "end": v(549.18, 2855.59) * mm});
            skLineSegment(sketch, "E213.left", {"start": v(299.18, 3105.59) * mm, "end": v(299.18, 2855.59) * mm});
            skLineSegment(sketch, "E213.right", {"start": v(549.18, 3105.59) * mm, "end": v(549.18, 2855.59) * mm});
            skLineSegment(sketch, "E214", {"start": v(424.18, 3031.13) * mm, "end": v(424.18, 2980.59) * mm, "construction": true});
            skLineSegment(sketch, "E215", {"start": v(424.18, 2980.59) * mm, "end": v(470.05, 2980.59) * mm, "construction": true});
            skCircle(sketch, "E216", {"center": v(334.18, 3070.59) * mm, "radius": 9 * mm});
            skCircle(sketch, "E217", {"center": v(334.18, 2890.59) * mm, "radius": 9 * mm});
            skCircle(sketch, "E218", {"center": v(514.18, 3070.59) * mm, "radius": 9 * mm});
            skCircle(sketch, "E219", {"center": v(514.18, 2890.59) * mm, "radius": 9 * mm});
            skLineSegment(sketch, "E220.bottom", {"start": v(3994.3, 2320.46) * mm, "end": v(4244.3, 2320.46) * mm});
            skLineSegment(sketch, "E220.top", {"start": v(3994.3, 2070.46) * mm, "end": v(4244.3, 2070.46) * mm});
            skLineSegment(sketch, "E220.left", {"start": v(3994.3, 2320.46) * mm, "end": v(3994.3, 2070.46) * mm});
            skLineSegment(sketch, "E220.right", {"start": v(4244.3, 2320.46) * mm, "end": v(4244.3, 2070.46) * mm});
            skLineSegment(sketch, "E221", {"start": v(4119.3, 2246.01) * mm, "end": v(4119.3, 2195.46) * mm, "construction": true});
            skLineSegment(sketch, "E222", {"start": v(4119.3, 2195.46) * mm, "end": v(4165.16, 2195.46) * mm, "construction": true});
            skCircle(sketch, "E223", {"center": v(4029.3, 2285.46) * mm, "radius": 9 * mm});
            skCircle(sketch, "E224", {"center": v(4029.3, 2105.46) * mm, "radius": 9 * mm});
            skCircle(sketch, "E225", {"center": v(4209.3, 2285.46) * mm, "radius": 9 * mm});
            skCircle(sketch, "E226", {"center": v(4209.3, 2105.46) * mm, "radius": 9 * mm});
            skLineSegment(sketch, "E227.bottom", {"start": v(-2607.42, 3706.25) * mm, "end": v(-2357.42, 3706.25) * mm});
            skLineSegment(sketch, "E227.top", {"start": v(-2607.42, 3456.25) * mm, "end": v(-2357.42, 3456.25) * mm});
            skLineSegment(sketch, "E227.left", {"start": v(-2607.42, 3706.25) * mm, "end": v(-2607.42, 3456.25) * mm});
            skLineSegment(sketch, "E227.right", {"start": v(-2357.42, 3706.25) * mm, "end": v(-2357.42, 3456.25) * mm});
            skLineSegment(sketch, "E228", {"start": v(-2482.42, 3631.8) * mm, "end": v(-2482.42, 3581.25) * mm, "construction": true});
            skLineSegment(sketch, "E229", {"start": v(-2482.42, 3581.25) * mm, "end": v(-2436.56, 3581.25) * mm, "construction": true});
            skCircle(sketch, "E230", {"center": v(-2572.42, 3671.25) * mm, "radius": 9 * mm});
            skCircle(sketch, "E231", {"center": v(-2572.42, 3491.25) * mm, "radius": 9 * mm});
            skCircle(sketch, "E232", {"center": v(-2392.42, 3671.25) * mm, "radius": 9 * mm});
            skCircle(sketch, "E233", {"center": v(-2392.42, 3491.25) * mm, "radius": 9 * mm});
            skLineSegment(sketch, "E234.bottom", {"start": v(-3627.34, 3765.26) * mm, "end": v(-3377.34, 3765.26) * mm});
            skLineSegment(sketch, "E234.top", {"start": v(-3627.34, 3515.26) * mm, "end": v(-3377.34, 3515.26) * mm});
            skLineSegment(sketch, "E234.left", {"start": v(-3627.34, 3765.26) * mm, "end": v(-3627.34, 3515.26) * mm});
            skLineSegment(sketch, "E234.right", {"start": v(-3377.34, 3765.26) * mm, "end": v(-3377.34, 3515.26) * mm});
            skLineSegment(sketch, "E235", {"start": v(-3502.34, 3690.8) * mm, "end": v(-3502.34, 3640.26) * mm, "construction": true});
            skLineSegment(sketch, "E236", {"start": v(-3502.34, 3640.26) * mm, "end": v(-3456.48, 3640.26) * mm, "construction": true});
            skCircle(sketch, "E237", {"center": v(-3592.34, 3730.26) * mm, "radius": 9 * mm});
            skCircle(sketch, "E238", {"center": v(-3592.34, 3550.26) * mm, "radius": 9 * mm});
            skCircle(sketch, "E239", {"center": v(-3412.34, 3730.26) * mm, "radius": 9 * mm});
            skCircle(sketch, "E240", {"center": v(-3412.34, 3550.26) * mm, "radius": 9 * mm});
            skSolve(sketch);
        }
        {
            var Q0;
            Q0 = qSketchRegion(id + "F15", true);
            extrude(context, id + "F16", {"entities" : qUnion([Q0]), "depth" : 10 * mm, "offsetDistance" : 25 * mm});
        }
        {
            var Q0;
            Q0=makeQuery(id+"F6.opExtrude","SWEPT_FACE",FACE,{"disambiguationData":[OSD([sQuery(id+"F5.wireOp",EDGE,"E22")])]});
            var sketch = newSketch(context, id + "F17", { "sketchPlane" : qUnion([Q0])});
            skLineSegment(sketch, "E241.bottom", {"start": v(-4950, 905) * mm, "end": v(-3650, 905) * mm});
            skLineSegment(sketch, "E241.top", {"start": v(-4950, -560) * mm, "end": v(-3650, -560) * mm});
            skLineSegment(sketch, "E241.left", {"start": v(-4950, 905) * mm, "end": v(-4950, -560) * mm});
            skLineSegment(sketch, "E241.right", {"start": v(-3650, 905) * mm, "end": v(-3650, -560) * mm});
            skSolve(sketch);
        }
        {
            var Q0;
            Q0 = qSketchRegion(id + "F17", true);
            extrude(context, id + "F18", {"entities" : qUnion([Q0]), "operationType" : NewBodyOperationType.REMOVE, "depth" : 400 * mm, "offsetDistance" : 25 * mm, "hasSecondDirection" : true, "secondDirectionOppositeDirection" : true, "secondDirectionDepth" : 200 * mm});
        }
        {
            var Q0;
            Q0 = qSketchRegion(id + "F17", true);
            extrude(context, id + "F19", {"entities" : qUnion([Q0]), "operationType" : NewBodyOperationType.REMOVE, "oppositeDirection" : true, "depth" : 250 * mm, "offsetDistance" : 25 * mm, "hasSecondDirection" : true, "secondDirectionOppositeDirection" : false, "secondDirectionDepth" : 200 * mm});
        }
        {
            var Q0;
            Q0=makeQuery(id+"F1.opExtrude","SWEPT_FACE",FACE,{"disambiguationData":[OSD([sQuery(id+"F0.wireOp",EDGE,"E1")])]});
            var sketch = newSketch(context, id + "F20", { "sketchPlane" : qUnion([Q0])});
            skLineSegment(sketch, "E242", {"start": v(-975, 2170) * mm, "end": v(-900, 2170) * mm});
            skLineSegment(sketch, "E243", {"start": v(-900, 2170) * mm, "end": v(-900, 2370) * mm});
            skLineSegment(sketch, "E244", {"start": v(-900, 2370) * mm, "end": v(-975, 2370) * mm});
            skLineSegment(sketch, "E245", {"start": v(-975, 2370) * mm, "end": v(-975, 2358) * mm});
            skLineSegment(sketch, "E246", {"start": v(-975, 2358) * mm, "end": v(-906, 2358) * mm});
            skLineSegment(sketch, "E247", {"start": v(-906, 2358) * mm, "end": v(-906, 2182) * mm});
            skLineSegment(sketch, "E248", {"start": v(-906, 2182) * mm, "end": v(-975, 2182) * mm});
            skLineSegment(sketch, "E249", {"start": v(-975, 2182) * mm, "end": v(-975, 2170) * mm});
            skLineSegment(sketch, "E250", {"start": v(-1200, 2288.38) * mm, "end": v(-1200, 2326.04) * mm, "construction": true});
            skLineSegment(sketch, "E251.MirrorCS", {"start": v(-1425, 2182) * mm, "end": v(-1425, 2170) * mm});
            skLineSegment(sketch, "E252.MirrorCS", {"start": v(-1425, 2370) * mm, "end": v(-1425, 2358) * mm});
            skLineSegment(sketch, "E253.MirrorCS", {"start": v(-1425, 2358) * mm, "end": v(-1494, 2358) * mm});
            skLineSegment(sketch, "E254.MirrorCS", {"start": v(-1500, 2370) * mm, "end": v(-1425, 2370) * mm});
            skLineSegment(sketch, "E255.MirrorCS", {"start": v(-1494, 2358) * mm, "end": v(-1494, 2182) * mm});
            skLineSegment(sketch, "E256.MirrorCS", {"start": v(-1425, 2170) * mm, "end": v(-1500, 2170) * mm});
            skLineSegment(sketch, "E257.MirrorCS", {"start": v(-1500, 2170) * mm, "end": v(-1500, 2370) * mm});
            skLineSegment(sketch, "E258.MirrorCS", {"start": v(-1494, 2182) * mm, "end": v(-1425, 2182) * mm});
            skLineSegment(sketch, "E259", {"start": v(1430, 2170) * mm, "end": v(1505, 2170) * mm});
            skLineSegment(sketch, "E260", {"start": v(1505, 2170) * mm, "end": v(1505, 2370) * mm});
            skLineSegment(sketch, "E261", {"start": v(1505, 2370) * mm, "end": v(1430, 2370) * mm});
            skLineSegment(sketch, "E262", {"start": v(1430, 2370) * mm, "end": v(1430, 2358) * mm});
            skLineSegment(sketch, "E263", {"start": v(1430, 2358) * mm, "end": v(1499, 2358) * mm});
            skLineSegment(sketch, "E264", {"start": v(1499, 2358) * mm, "end": v(1499, 2182) * mm});
            skLineSegment(sketch, "E265", {"start": v(1499, 2182) * mm, "end": v(1430, 2182) * mm});
            skLineSegment(sketch, "E266", {"start": v(1430, 2182) * mm, "end": v(1430, 2170) * mm});
            skLineSegment(sketch, "E267", {"start": v(1505, 2170) * mm, "end": v(1360, 2170) * mm, "construction": true});
            skLineSegment(sketch, "E268", {"start": v(1360, 2170) * mm, "end": v(1360, 2317.34) * mm, "construction": true});
            skLineSegment(sketch, "E269.MirrorCS", {"start": v(1290, 2182) * mm, "end": v(1290, 2170) * mm});
            skLineSegment(sketch, "E270.MirrorCS", {"start": v(1290, 2370) * mm, "end": v(1290, 2358) * mm});
            skLineSegment(sketch, "E271.MirrorCS", {"start": v(1290, 2358) * mm, "end": v(1221, 2358) * mm});
            skLineSegment(sketch, "E272.MirrorCS", {"start": v(1215, 2370) * mm, "end": v(1290, 2370) * mm});
            skLineSegment(sketch, "E273.MirrorCS", {"start": v(1221, 2358) * mm, "end": v(1221, 2182) * mm});
            skLineSegment(sketch, "E274.MirrorCS", {"start": v(1290, 2170) * mm, "end": v(1215, 2170) * mm});
            skLineSegment(sketch, "E275.MirrorCS", {"start": v(1215, 2170) * mm, "end": v(1215, 2370) * mm});
            skLineSegment(sketch, "E276.MirrorCS", {"start": v(1221, 2182) * mm, "end": v(1290, 2182) * mm});
            skSolve(sketch);
        }
        {
            var Q0;
            Q0 = qSketchRegion(id + "F20", true);
            extrude(context, id + "F21", {"entities" : qUnion([Q0]), "depth" : 350 * mm, "offsetDistance" : 25 * mm});
        }
        {
            var Q0;
            Q0=makeQuery(id+"F6.opExtrude","SWEPT_FACE",FACE,{"disambiguationData":[OSD([sQuery(id+"F5.wireOp",EDGE,"E18")])]});
            cPlane(context, id + "F22", {"entities" : qUnion([Q0]), "cplaneType" : CPlaneType.OFFSET, "offset" : 1000 * mm, "oppositeDirection" : true, "width" : 150 * mm, "height" : 150 * mm});
        }
        {
            var Q0;
            Q0=makeQuery(id+"F6.opExtrude","SWEPT_FACE",FACE,{"disambiguationData":[OSD([sQuery(id+"F5.wireOp",EDGE,"E18")])]});
            var Q1;
            Q1=makeQuery(id+"F6.opExtrude","SWEPT_EDGE",EDGE,{"disambiguationData":[OSD([sQuery(id+"F5.wireOp",EDGE,"E17"),sQuery(id+"F5.wireOp",EDGE,"E18")])]});
            cPlane(context, id + "F23", {"entities" : qUnion([Q0, Q1]), "cplaneType" : CPlaneType.LINE_ANGLE, "offset" : 25 * mm, "angle" : 12 * degree, "oppositeDirection" : true, "width" : 150 * mm, "height" : 150 * mm});
        }
        {
            var Q0;
            Q0=qCreatedBy(id+"F22.planeOp",FACE);
            var sketch = newSketch(context, id + "F24", { "sketchPlane" : qUnion([Q0])});
            skLineSegment(sketch, "E277", {"start": v(-860, 3840.23) * mm, "end": v(-900, 3840.23) * mm, "construction": true});
            skLineSegment(sketch, "E278", {"start": v(-975, 3078.32) * mm, "end": v(-900, 3078.32) * mm});
            skLineSegment(sketch, "E279", {"start": v(-900, 3078.32) * mm, "end": v(-900, 3278.32) * mm});
            skLineSegment(sketch, "E280", {"start": v(-900, 3278.32) * mm, "end": v(-975, 3278.32) * mm});
            skLineSegment(sketch, "E281", {"start": v(-975, 3278.32) * mm, "end": v(-975, 3266.32) * mm});
            skLineSegment(sketch, "E282", {"start": v(-975, 3266.32) * mm, "end": v(-906, 3266.32) * mm});
            skLineSegment(sketch, "E283", {"start": v(-906, 3266.32) * mm, "end": v(-906, 3090.32) * mm});
            skLineSegment(sketch, "E284", {"start": v(-906, 3090.32) * mm, "end": v(-975, 3090.32) * mm});
            skLineSegment(sketch, "E285", {"start": v(-975, 3090.32) * mm, "end": v(-975, 3078.32) * mm});
            skLineSegment(sketch, "E286", {"start": v(-1200, 3195.1) * mm, "end": v(-1200, 3232.75) * mm, "construction": true});
            skLineSegment(sketch, "E287.MirrorCS", {"start": v(-1425, 3090.32) * mm, "end": v(-1425, 3078.32) * mm});
            skLineSegment(sketch, "E288.MirrorCS", {"start": v(-1425, 3278.32) * mm, "end": v(-1425, 3266.32) * mm});
            skLineSegment(sketch, "E289.MirrorCS", {"start": v(-1425, 3266.32) * mm, "end": v(-1494, 3266.32) * mm});
            skLineSegment(sketch, "E290.MirrorCS", {"start": v(-1500, 3278.32) * mm, "end": v(-1425, 3278.32) * mm});
            skLineSegment(sketch, "E291.MirrorCS", {"start": v(-1494, 3266.32) * mm, "end": v(-1494, 3090.32) * mm});
            skLineSegment(sketch, "E292.MirrorCS", {"start": v(-1425, 3078.32) * mm, "end": v(-1500, 3078.32) * mm});
            skLineSegment(sketch, "E293.MirrorCS", {"start": v(-1500, 3078.32) * mm, "end": v(-1500, 3278.32) * mm});
            skLineSegment(sketch, "E294.MirrorCS", {"start": v(-1494, 3090.32) * mm, "end": v(-1425, 3090.32) * mm});
            skLineSegment(sketch, "E295", {"start": v(1430, 3078.32) * mm, "end": v(1505, 3078.32) * mm});
            skLineSegment(sketch, "E296", {"start": v(1505, 3078.32) * mm, "end": v(1505, 3278.32) * mm});
            skLineSegment(sketch, "E297", {"start": v(1505, 3278.32) * mm, "end": v(1430, 3278.32) * mm});
            skLineSegment(sketch, "E298", {"start": v(1430, 3278.32) * mm, "end": v(1430, 3266.32) * mm});
            skLineSegment(sketch, "E299", {"start": v(1430, 3266.32) * mm, "end": v(1499, 3266.32) * mm});
            skLineSegment(sketch, "E300", {"start": v(1499, 3266.32) * mm, "end": v(1499, 3090.32) * mm});
            skLineSegment(sketch, "E301", {"start": v(1499, 3090.32) * mm, "end": v(1430, 3090.32) * mm});
            skLineSegment(sketch, "E302", {"start": v(1430, 3090.32) * mm, "end": v(1430, 3078.32) * mm});
            skLineSegment(sketch, "E303", {"start": v(1505, 3078.32) * mm, "end": v(1361.5, 3078.32) * mm, "construction": true});
            skLineSegment(sketch, "E304", {"start": v(1361.5, 3078.32) * mm, "end": v(1361.5, 4073.37) * mm, "construction": true});
            skLineSegment(sketch, "E305.MirrorCS", {"start": v(1293, 3090.32) * mm, "end": v(1293, 3078.32) * mm});
            skLineSegment(sketch, "E306.MirrorCS", {"start": v(1293, 3278.32) * mm, "end": v(1293, 3266.32) * mm});
            skLineSegment(sketch, "E307.MirrorCS", {"start": v(1293, 3266.32) * mm, "end": v(1224, 3266.32) * mm});
            skLineSegment(sketch, "E308.MirrorCS", {"start": v(1218, 3278.32) * mm, "end": v(1293, 3278.32) * mm});
            skLineSegment(sketch, "E309.MirrorCS", {"start": v(1224, 3266.32) * mm, "end": v(1224, 3090.32) * mm});
            skLineSegment(sketch, "E310.MirrorCS", {"start": v(1293, 3078.32) * mm, "end": v(1218, 3078.32) * mm});
            skLineSegment(sketch, "E311.MirrorCS", {"start": v(1218, 3078.32) * mm, "end": v(1218, 3278.32) * mm});
            skLineSegment(sketch, "E312.MirrorCS", {"start": v(1224, 3090.32) * mm, "end": v(1293, 3090.32) * mm});
            skLineSegment(sketch, "E313", {"start": v(-860, 3078.32) * mm, "end": v(-900, 3078.32) * mm});
            skLineSegment(sketch, "E314", {"start": v(-900, 3078.32) * mm, "end": v(1505, 3078.32) * mm, "construction": true});
            skSolve(sketch);
        }
        {
            var Q0;
            Q0 = qSketchRegion(id + "F24", true);
            var Q1;
            Q1=makeQuery(id+"F21.opExtrude","CAP_FACE",FACE,{"disambiguationData":[OSD([sQuery(id+"F20.wireOp",EDGE,"E242"),sQuery(id+"F20.wireOp",EDGE,"E243"),sQuery(id+"F20.wireOp",EDGE,"E244"),sQuery(id+"F20.wireOp",EDGE,"E245"),sQuery(id+"F20.wireOp",EDGE,"E246"),sQuery(id+"F20.wireOp",EDGE,"E247"),sQuery(id+"F20.wireOp",EDGE,"E248"),sQuery(id+"F20.wireOp",EDGE,"E249")])],"isStart":false});
            extrude(context, id + "F25", {"entities" : qUnion([Q0]), "endBound" : BoundingType.UP_TO_SURFACE, "oppositeDirection" : true, "depth" : 500 * mm, "endBoundEntityFace" : qUnion([Q1]), "offsetDistance" : 25 * mm});
        }
        {
            var Q0;
            Q0=makeQuery(id+"F1.opExtrude","SWEPT_FACE",FACE,{"disambiguationData":[OSD([sQuery(id+"F0.wireOp",EDGE,"E2")])]});
            var sketch = newSketch(context, id + "F26", { "sketchPlane" : qUnion([Q0])});
            skLineSegment(sketch, "E315", {"start": v(4878.53, 1970) * mm, "end": v(4953.53, 1970) * mm});
            skLineSegment(sketch, "E316", {"start": v(4953.53, 1970) * mm, "end": v(4953.53, 2170) * mm});
            skLineSegment(sketch, "E317", {"start": v(4953.53, 2170) * mm, "end": v(4878.53, 2170) * mm});
            skLineSegment(sketch, "E318", {"start": v(4878.53, 2170) * mm, "end": v(4878.53, 2158) * mm});
            skLineSegment(sketch, "E319", {"start": v(4878.53, 2158) * mm, "end": v(4947.53, 2158) * mm});
            skLineSegment(sketch, "E320", {"start": v(4947.53, 2158) * mm, "end": v(4947.53, 1982) * mm});
            skLineSegment(sketch, "E321", {"start": v(4947.53, 1982) * mm, "end": v(4878.53, 1982) * mm});
            skLineSegment(sketch, "E322", {"start": v(4878.53, 1982) * mm, "end": v(4878.53, 1970) * mm});
            skSolve(sketch);
        }
        {
            var Q0;
            Q0 = qSketchRegion(id + "F26", true);
            extrude(context, id + "F27", {"entities" : qUnion([Q0]), "depth" : 975 * mm, "offsetDistance" : 25 * mm});
        }
        {
            var Q0;
            Q0=makeQuery(id+"F1.opExtrude","SWEPT_FACE",FACE,{"disambiguationData":[OSD([sQuery(id+"F0.wireOp",EDGE,"E0")])]});
            var sketch = newSketch(context, id + "F28", { "sketchPlane" : qUnion([Q0])});
            skLineSegment(sketch, "E323.MirrorCS", {"start": v(-4875.05, 1982.12) * mm, "end": v(-4875.05, 1970.13) * mm});
            skLineSegment(sketch, "E324.MirrorCS", {"start": v(-4875.05, 2170) * mm, "end": v(-4875.05, 2158) * mm});
            skLineSegment(sketch, "E325.MirrorCS", {"start": v(-4875.05, 2158) * mm, "end": v(-4944, 2158) * mm});
            skLineSegment(sketch, "E326.MirrorCS", {"start": v(-4950, 2170) * mm, "end": v(-4875.05, 2170) * mm});
            skLineSegment(sketch, "E327.MirrorCS", {"start": v(-4944, 2158) * mm, "end": v(-4944, 1982.12) * mm});
            skLineSegment(sketch, "E328.MirrorCS", {"start": v(-4875.05, 1970.13) * mm, "end": v(-4950, 1970.13) * mm});
            skLineSegment(sketch, "E329.MirrorCS", {"start": v(-4950, 1970.13) * mm, "end": v(-4950, 2170) * mm});
            skLineSegment(sketch, "E330.MirrorCS", {"start": v(-4944, 1982.12) * mm, "end": v(-4875.05, 1982.12) * mm});
            skSolve(sketch);
        }
        {
            var Q0;
            Q0 = qSketchRegion(id + "F28", true);
            extrude(context, id + "F29", {"entities" : qUnion([Q0]), "depth" : 630 * mm, "offsetDistance" : 25 * mm});
        }
        {
            var Q0;
            Q0=qCreatedBy(id+"F23.planeOp",FACE);
            var sketch = newSketch(context, id + "F30", { "sketchPlane" : qUnion([Q0])});
            skLineSegment(sketch, "E331", {"start": v(0, 0) * mm, "end": v(0, 3714) * mm, "construction": true});
            skLineSegment(sketch, "E332", {"start": v(0, 3714) * mm, "end": v(900, 3714) * mm, "construction": true});
            skLineSegment(sketch, "E333", {"start": v(1425, 3714) * mm, "end": v(1500, 3714) * mm});
            skLineSegment(sketch, "E334", {"start": v(1500, 3714) * mm, "end": v(1500, 3914) * mm});
            skLineSegment(sketch, "E335", {"start": v(1500, 3914) * mm, "end": v(1425, 3914) * mm});
            skLineSegment(sketch, "E336", {"start": v(1425, 3914) * mm, "end": v(1425, 3902) * mm});
            skLineSegment(sketch, "E337", {"start": v(1425, 3902) * mm, "end": v(1494, 3902) * mm});
            skLineSegment(sketch, "E338", {"start": v(1494, 3902) * mm, "end": v(1494, 3726) * mm});
            skLineSegment(sketch, "E339", {"start": v(1494, 3726) * mm, "end": v(1425, 3726) * mm});
            skLineSegment(sketch, "E340", {"start": v(1425, 3726) * mm, "end": v(1425, 3714) * mm});
            skLineSegment(sketch, "E341", {"start": v(1200, 3830.78) * mm, "end": v(1200, 3868.43) * mm, "construction": true});
            skLineSegment(sketch, "E342.MirrorCS", {"start": v(975, 3726) * mm, "end": v(975, 3714) * mm});
            skLineSegment(sketch, "E343.MirrorCS", {"start": v(975, 3914) * mm, "end": v(975, 3902) * mm});
            skLineSegment(sketch, "E344.MirrorCS", {"start": v(975, 3902) * mm, "end": v(906, 3902) * mm});
            skLineSegment(sketch, "E345.MirrorCS", {"start": v(900, 3914) * mm, "end": v(975, 3914) * mm});
            skLineSegment(sketch, "E346.MirrorCS", {"start": v(906, 3902) * mm, "end": v(906, 3726) * mm});
            skLineSegment(sketch, "E347.MirrorCS", {"start": v(975, 3714) * mm, "end": v(900, 3714) * mm});
            skLineSegment(sketch, "E348.MirrorCS", {"start": v(900, 3714) * mm, "end": v(900, 3914) * mm});
            skLineSegment(sketch, "E349.MirrorCS", {"start": v(906, 3726) * mm, "end": v(975, 3726) * mm});
            skLineSegment(sketch, "E350", {"start": v(-1293, 3714) * mm, "end": v(-1218, 3714) * mm});
            skLineSegment(sketch, "E351", {"start": v(-1218, 3714) * mm, "end": v(-1218, 3914) * mm});
            skLineSegment(sketch, "E352", {"start": v(-1218, 3914) * mm, "end": v(-1293, 3914) * mm});
            skLineSegment(sketch, "E353", {"start": v(-1293, 3914) * mm, "end": v(-1293, 3902) * mm});
            skLineSegment(sketch, "E354", {"start": v(-1293, 3902) * mm, "end": v(-1224, 3902) * mm});
            skLineSegment(sketch, "E355", {"start": v(-1224, 3902) * mm, "end": v(-1224, 3726) * mm});
            skLineSegment(sketch, "E356", {"start": v(-1224, 3726) * mm, "end": v(-1293, 3726) * mm});
            skLineSegment(sketch, "E357", {"start": v(-1293, 3726) * mm, "end": v(-1293, 3714) * mm});
            skLineSegment(sketch, "E358", {"start": v(-1218, 3714) * mm, "end": v(-1361.5, 3714) * mm, "construction": true});
            skLineSegment(sketch, "E359", {"start": v(-1361.5, 3714) * mm, "end": v(-1361.5, 4713.17) * mm, "construction": true});
            skLineSegment(sketch, "E360.MirrorCS", {"start": v(-1430, 3726) * mm, "end": v(-1430, 3714) * mm});
            skLineSegment(sketch, "E361.MirrorCS", {"start": v(-1430, 3914) * mm, "end": v(-1430, 3902) * mm});
            skLineSegment(sketch, "E362.MirrorCS", {"start": v(-1430, 3902) * mm, "end": v(-1499, 3902) * mm});
            skLineSegment(sketch, "E363.MirrorCS", {"start": v(-1505, 3914) * mm, "end": v(-1430, 3914) * mm});
            skLineSegment(sketch, "E364.MirrorCS", {"start": v(-1499, 3902) * mm, "end": v(-1499, 3726) * mm});
            skLineSegment(sketch, "E365.MirrorCS", {"start": v(-1430, 3714) * mm, "end": v(-1505, 3714) * mm});
            skLineSegment(sketch, "E366.MirrorCS", {"start": v(-1505, 3714) * mm, "end": v(-1505, 3914) * mm});
            skLineSegment(sketch, "E367.MirrorCS", {"start": v(-1499, 3726) * mm, "end": v(-1430, 3726) * mm});
            skLineSegment(sketch, "E368", {"start": v(1540, 3714) * mm, "end": v(1500, 3714) * mm});
            skLineSegment(sketch, "E369", {"start": v(-1218, 3714) * mm, "end": v(1500, 3714) * mm, "construction": true});
            skSolve(sketch);
        }
        {
            var Q0;
            Q0 = qSketchRegion(id + "F30", true);
            var Q1;
            Q1=makeQuery(id+"F25.opExtrude","CAP_FACE",FACE,{"disambiguationData":[OSD([sQuery(id+"F24.wireOp",EDGE,"E287.MirrorCS"),sQuery(id+"F24.wireOp",EDGE,"E288.MirrorCS"),sQuery(id+"F24.wireOp",EDGE,"E289.MirrorCS"),sQuery(id+"F24.wireOp",EDGE,"E290.MirrorCS"),sQuery(id+"F24.wireOp",EDGE,"E291.MirrorCS"),sQuery(id+"F24.wireOp",EDGE,"E292.MirrorCS"),sQuery(id+"F24.wireOp",EDGE,"E293.MirrorCS"),sQuery(id+"F24.wireOp",EDGE,"E294.MirrorCS")])],"isStart":true});
            extrude(context, id + "F31", {"entities" : qUnion([Q0]), "endBound" : BoundingType.UP_TO_SURFACE, "depth" : 25 * mm, "endBoundEntityFace" : qUnion([Q1]), "offsetDistance" : 25 * mm});
        }
        {
            var Q0;
            Q0=makeQuery(id+"F31.opExtrude","SWEPT_FACE",FACE,{"disambiguationData":[OSD([sQuery(id+"F30.wireOp",EDGE,"E338")])]});
            var sketch = newSketch(context, id + "F32", { "sketchPlane" : qUnion([Q0])});
            skLineSegment(sketch, "E370.bottom", {"start": v(-3560.65, 3902) * mm, "end": v(-3550.65, 3902) * mm});
            skLineSegment(sketch, "E370.top", {"start": v(-3560.65, 3726) * mm, "end": v(-3550.65, 3726) * mm});
            skLineSegment(sketch, "E370.left", {"start": v(-3560.65, 3902) * mm, "end": v(-3560.65, 3726) * mm});
            skLineSegment(sketch, "E370.right", {"start": v(-3550.65, 3902) * mm, "end": v(-3550.65, 3726) * mm});
            skSolve(sketch);
        }
        {
            var Q0;
            Q0 = qSketchRegion(id + "F32", true);
            var Q1;
            Q1=makeQuery(id+"F31.opExtrude","SWEPT_FACE",FACE,{"disambiguationData":[OSD([sQuery(id+"F30.wireOp",EDGE,"E346.MirrorCS")])]});
            extrude(context, id + "F33", {"entities" : qUnion([Q0]), "endBound" : BoundingType.UP_TO_SURFACE, "depth" : 500 * mm, "endBoundEntityFace" : qUnion([Q1]), "offsetDistance" : 25 * mm});
        }
        {
            var Q0;
            Q0=makeQuery(id+"F31.opExtrude","SWEPT_FACE",FACE,{"disambiguationData":[OSD([sQuery(id+"F30.wireOp",EDGE,"E355")])]});
            var sketch = newSketch(context, id + "F34", { "sketchPlane" : qUnion([Q0])});
            skLineSegment(sketch, "E371.bottom", {"start": v(-3560.65, 3902) * mm, "end": v(-3550.65, 3902) * mm});
            skLineSegment(sketch, "E371.top", {"start": v(-3560.65, 3726) * mm, "end": v(-3550.65, 3726) * mm});
            skLineSegment(sketch, "E371.left", {"start": v(-3560.65, 3902) * mm, "end": v(-3560.65, 3726) * mm});
            skLineSegment(sketch, "E371.right", {"start": v(-3550.65, 3902) * mm, "end": v(-3550.65, 3726) * mm});
            skSolve(sketch);
        }
        {
            var Q0;
            Q0 = qSketchRegion(id + "F34", true);
            var Q1;
            Q1=makeQuery(id+"F31.opExtrude","SWEPT_FACE",FACE,{"disambiguationData":[OSD([sQuery(id+"F30.wireOp",EDGE,"E364.MirrorCS")])]});
            extrude(context, id + "F35", {"entities" : qUnion([Q0]), "endBound" : BoundingType.UP_TO_SURFACE, "depth" : 500 * mm, "endBoundEntityFace" : qUnion([Q1]), "offsetDistance" : 25 * mm});
        }
        {
            var Q0;
            Q0=makeQuery(id+"F33.opExtrude","SWEPT_FACE",FACE,{"disambiguationData":[OSD([sQuery(id+"F32.wireOp",EDGE,"E370.left")])]});
            var sketch = newSketch(context, id + "F36", { "sketchPlane" : qUnion([Q0])});
            skCircle(sketch, "E372", {"center": v(-1211.04, 3818.01) * mm, "radius": 17.5 * mm});
            skCircle(sketch, "E373", {"center": v(1365, 3818.01) * mm, "radius": 17.5 * mm});
            skSolve(sketch);
        }
        {
            var Q0;
            Q0=makeQuery(id+"F31.opExtrude","SWEPT_FACE",FACE,{"disambiguationData":[OSD([sQuery(id+"F30.wireOp",EDGE,"E334")])]});
            var sketch = newSketch(context, id + "F37", { "sketchPlane" : qUnion([Q0])});
            skLineSegment(sketch, "E374", {"start": v(3560.65, 3814) * mm, "end": v(3610.65, 3814) * mm});
            skLineSegment(sketch, "E375", {"start": v(3660.65, 3864) * mm, "end": v(3660.65, 4864) * mm});
            skPoint(sketch, "E376.visualSharp", {"position": v(3660.65, 3814) * mm});
            skArc(sketch, "E376.filletArc", {"start": v(3610.65, 3814) * mm, "mid": v(3646, 3828.64) * mm, "end": v(3660.65, 3864) * mm});
            skSolve(sketch);
        }
        {
            var Q0;
            Q0 = qSketchRegion(id + "F36", true);
            var Q1;
            Q1 = qConstructionFilter(qBodyType(qCreatedBy(id + "F37" ,EDGE), BodyType.WIRE), ConstructionObject.NO);
            sweep(context, id + "F38", {"profiles" : qUnion([Q0]), "path" : qUnion([Q1])});
        }
        {
            var Q0;
            Q0=makeQuery(id+"F31.opExtrude","SWEPT_FACE",FACE,{"disambiguationData":[OSD([sQuery(id+"F30.wireOp",EDGE,"E334")])]});
            cPlane(context, id + "F39", {"entities" : qUnion([Q0]), "cplaneType" : CPlaneType.OFFSET, "offset" : 300 * mm, "oppositeDirection" : true, "width" : 150 * mm, "height" : 150 * mm});
        }
        {
            var Q0;
            Q0=qCreatedBy(id+"F39.planeOp",FACE);
            var sketch = newSketch(context, id + "F40", { "sketchPlane" : qUnion([Q0])});
            skCircle(sketch, "E377", {"center": v(3660.65, 4864) * mm, "radius": 17.5 * mm});
            skSolve(sketch);
        }
        {
            var Q0;
            Q0=makeQuery(id+"F33.opExtrude","SWEPT_FACE",FACE,{"disambiguationData":[OSD([sQuery(id+"F32.wireOp",EDGE,"E370.left")])]});
            var sketch = newSketch(context, id + "F41", { "sketchPlane" : qUnion([Q0])});
            skLineSegment(sketch, "E378", {"start": v(-1194, 4846.05) * mm, "end": v(-1034, 4846.05) * mm});
            skPoint(sketch, "E378.startSnap0", {"position": v(-1194, 4002) * mm});
            skLineSegment(sketch, "E379", {"start": v(-894, 4706.05) * mm, "end": v(-894, 4386.05) * mm});
            skLineSegment(sketch, "E380", {"start": v(-1034, 4246.05) * mm, "end": v(-1354, 4246.05) * mm});
            skLineSegment(sketch, "E381", {"start": v(-1494, 4386.05) * mm, "end": v(-1494, 4706.05) * mm});
            skLineSegment(sketch, "E382", {"start": v(-1354, 4846.05) * mm, "end": v(-1194, 4846.05) * mm});
            skArc(sketch, "E383.filletArc", {"start": v(-894, 4706.05) * mm, "mid": v(-935, 4805.05) * mm, "end": v(-1034, 4846.05) * mm});
            skArc(sketch, "E384.filletArc", {"start": v(-1034, 4246.05) * mm, "mid": v(-935, 4287.06) * mm, "end": v(-894, 4386.05) * mm});
            skArc(sketch, "E385.filletArc", {"start": v(-1494, 4386.05) * mm, "mid": v(-1453, 4287.06) * mm, "end": v(-1354, 4246.05) * mm});
            skArc(sketch, "E386.filletArc", {"start": v(-1354, 4846.05) * mm, "mid": v(-1453, 4805.05) * mm, "end": v(-1494, 4706.05) * mm});
            skSolve(sketch);
        }
        {
            var Q0;
            Q0 = qSketchRegion(id + "F40", true);
            var Q1;
            Q1 = qConstructionFilter(qBodyType(qCreatedBy(id + "F41" ,EDGE), BodyType.WIRE), ConstructionObject.NO);
            sweep(context, id + "F42", {"operationType" : NewBodyOperationType.ADD, "profiles" : qUnion([Q0]), "path" : qUnion([Q1])});
        }
        {
            var Q0;
            Q0=makeQuery(id+"F31.opExtrude","SWEPT_FACE",FACE,{"disambiguationData":[OSD([sQuery(id+"F30.wireOp",EDGE,"E366.MirrorCS")])]});
            cPlane(context, id + "F43", {"entities" : qUnion([Q0]), "cplaneType" : CPlaneType.OFFSET, "offset" : 143.5 * mm, "oppositeDirection" : true, "width" : 150 * mm, "height" : 150 * mm});
        }
        {
            var Q0;
            Q0=qCreatedBy(id+"F43.planeOp",FACE);
            var sketch = newSketch(context, id + "F44", { "sketchPlane" : qUnion([Q0])});
            skCircle(sketch, "E387", {"center": v(-3656.6, 4863.93) * mm, "radius": 17.5 * mm});
            skSolve(sketch);
        }
        {
            var Q0;
            Q0=makeQuery(id+"F35.opExtrude","SWEPT_FACE",FACE,{"disambiguationData":[OSD([sQuery(id+"F34.wireOp",EDGE,"E371.left")])]});
            var sketch = newSketch(context, id + "F45", { "sketchPlane" : qUnion([Q0])});
            skLineSegment(sketch, "E388", {"start": v(1279.07, 4835.47) * mm, "end": v(1429.07, 4835.47) * mm});
            skLineSegment(sketch, "E389", {"start": v(1479.07, 4785.47) * mm, "end": v(1479.07, 4485.47) * mm});
            skLineSegment(sketch, "E390", {"start": v(1429.07, 4435.47) * mm, "end": v(1279.07, 4435.47) * mm});
            skLineSegment(sketch, "E391", {"start": v(1229.07, 4485.47) * mm, "end": v(1229.07, 4785.47) * mm});
            skPoint(sketch, "E392.visualSharp", {"position": v(1229.07, 4835.47) * mm});
            skArc(sketch, "E392.filletArc", {"start": v(1279.07, 4835.47) * mm, "mid": v(1243.72, 4820.82) * mm, "end": v(1229.07, 4785.47) * mm});
            skPoint(sketch, "E393.visualSharp", {"position": v(1479.07, 4835.47) * mm});
            skArc(sketch, "E393.filletArc", {"start": v(1479.07, 4785.47) * mm, "mid": v(1464.43, 4820.82) * mm, "end": v(1429.07, 4835.47) * mm});
            skPoint(sketch, "E394.visualSharp", {"position": v(1479.07, 4435.47) * mm});
            skArc(sketch, "E394.filletArc", {"start": v(1429.07, 4435.47) * mm, "mid": v(1464.43, 4450.11) * mm, "end": v(1479.07, 4485.47) * mm});
            skPoint(sketch, "E395.visualSharp", {"position": v(1229.07, 4435.47) * mm});
            skArc(sketch, "E395.filletArc", {"start": v(1229.07, 4485.47) * mm, "mid": v(1243.72, 4450.11) * mm, "end": v(1279.07, 4435.47) * mm});
            skSolve(sketch);
        }
        {
            var Q0;
            Q0 = qSketchRegion(id + "F44", true);
            var Q1;
            Q1 = qConstructionFilter(qBodyType(qCreatedBy(id + "F45" ,EDGE), BodyType.WIRE), ConstructionObject.NO);
            sweep(context, id + "F46", {"operationType" : NewBodyOperationType.ADD, "profiles" : qUnion([Q0]), "path" : qUnion([Q1])});
        }
    });
